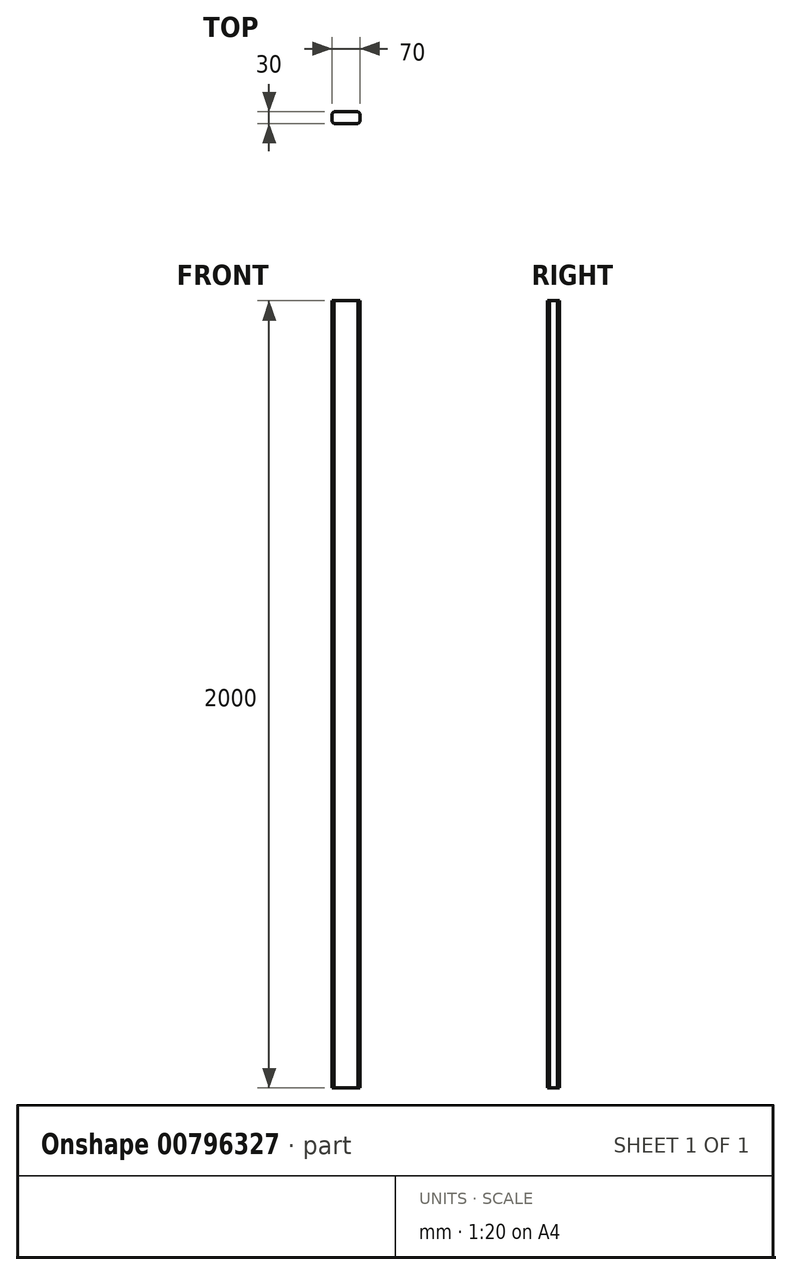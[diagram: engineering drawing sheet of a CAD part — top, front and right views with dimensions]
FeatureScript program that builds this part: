
annotation { "Feature Type Name" : "Feature", "Feature Type Description" : "" }
export const myFeature = defineFeature(function(context is Context, id is Id, definition is map)
    precondition{}
    {
        {
            var Q0;
            Q0=qCreatedBy(makeId("Top.planeOp"),FACE);
            var sketch = newSketch(context, id + "F0", { "sketchPlane" : qUnion([Q0])});
            skLineSegment(sketch, "E0.bottom", {"start": v(-23.02, 0) * mm, "end": v(46.98, 0) * mm});
            skLineSegment(sketch, "E0.top", {"start": v(-23.02, -30) * mm, "end": v(46.98, -30) * mm});
            skLineSegment(sketch, "E0.left", {"start": v(-23.02, 0) * mm, "end": v(-23.02, -30) * mm});
            skLineSegment(sketch, "E0.right", {"start": v(46.98, 0) * mm, "end": v(46.98, -30) * mm});
            skSolve(sketch);
        }
        {
            var Q0;
            Q0 = qSketchRegion(id + "F0", true);
            extrude(context, id + "F1", {"entities" : qUnion([Q0]), "depth" : 2000 * mm, "offsetDistance" : 25 * mm});
        }
        {
            var Q0;
            Q0=makeQuery(id+"F1.opExtrude","SWEPT_EDGE",EDGE,{"disambiguationData":[OSD([sQuery(id+"F0.wireOp",EDGE,"E0.top"),sQuery(id+"F0.wireOp",EDGE,"E0.left")])]});
            var Q1;
            Q1=makeQuery(id+"F1.opExtrude","SWEPT_EDGE",EDGE,{"disambiguationData":[OSD([sQuery(id+"F0.wireOp",EDGE,"E0.top"),sQuery(id+"F0.wireOp",EDGE,"E0.right")])]});
            var Q2;
            Q2=makeQuery(id+"F1.opExtrude","SWEPT_EDGE",EDGE,{"disambiguationData":[OSD([sQuery(id+"F0.wireOp",EDGE,"E0.bottom"),sQuery(id+"F0.wireOp",EDGE,"E0.left")])]});
            var Q3;
            Q3=makeQuery(id+"F1.opExtrude","SWEPT_EDGE",EDGE,{"disambiguationData":[OSD([sQuery(id+"F0.wireOp",EDGE,"E0.bottom"),sQuery(id+"F0.wireOp",EDGE,"E0.right")])]});
            chamfer(context, id + "F2", {"entities" : qUnion([Q0, Q1, Q2, Q3]), "width" : 5 * mm, "tangentPropagation" : true});
        }
        {
            var Q0;
            Q0=makeQuery(id+"F1.opExtrude","CAP_FACE",FACE,{"disambiguationData":[OSD([sQuery(id+"F0.wireOp",EDGE,"E0.bottom"),sQuery(id+"F0.wireOp",EDGE,"E0.top"),sQuery(id+"F0.wireOp",EDGE,"E0.left"),sQuery(id+"F0.wireOp",EDGE,"E0.right")])],"isStart":false});
            extrude(context, id + "F3", {"entities" : qUnion([Q0]), "operationType" : NewBodyOperationType.ADD, "oppositeDirection" : true, "depth" : 1047 * mm, "offsetDistance" : 25 * mm});
        }
    });
